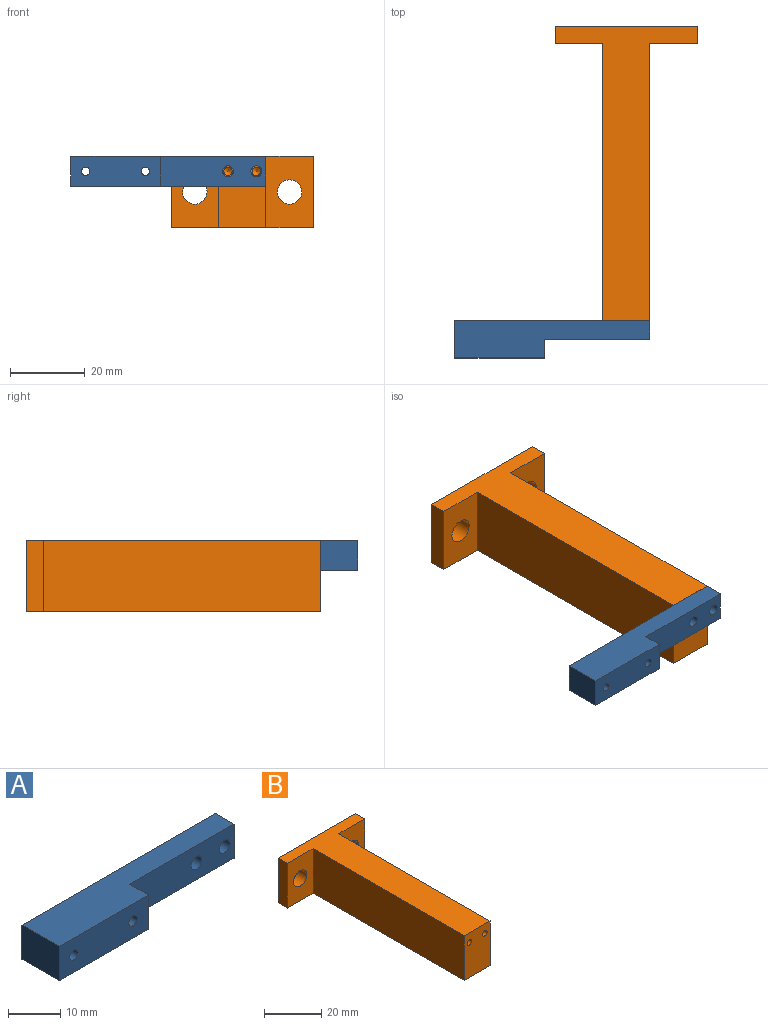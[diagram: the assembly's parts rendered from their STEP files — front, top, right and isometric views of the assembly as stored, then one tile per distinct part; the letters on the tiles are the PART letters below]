
ASSEMBLY  parts=2 mates=1
PART A: 12 faces, bbox 52.3x10x8 mm
  f0: plane 8x5mm, normal (1,0,0), area 40mm2, adj f1,f2,f3,f4
  f1: plane 52.32x10.01mm, normal (0,0,1), area 382.6mm2, adj f0,f3,f4,f5,f6,f7
  f2: plane 52.32x10.01mm, normal (0,0,-1), area 382.6mm2, adj f0,f3,f4,f5,f6,f7
  f3: plane 28.19x8mm, normal (0,-1,0), area 211.9mm2, adj f0,f1,f2,f5,f10,f11
  f4: plane 52.32x8mm, normal (0,1,0), area 397mm2, adj f0,f1,f2,f6,f8,f9,f10,f11
  f5: plane 8x5mm, normal (1,0,0), area 40mm2, adj f1,f2,f3,f7
  f6: plane 10.01x8mm, normal (-1,0,0), area 80.1mm2, adj f1,f2,f4,f7
  f7: plane 24.13x8mm, normal (0,-1,0), area 185mm2, adj f1,f2,f5,f6,f8,f9
  f8: cylinder r=1.13mm len=10.01mm, axis (0,1,0), area 71.1mm2, adj f4,f7
  f9: cylinder r=1.13mm len=10.01mm, axis (0,1,0), area 71.1mm2, adj f4,f7
  f10: cylinder r=1.47mm len=5mm, axis (0,-1,0), area 46.3mm2, adj f3,f4
  f11: cylinder r=1.47mm len=5mm, axis (0,-1,0), area 46.3mm2, adj f3,f4
PART B: 16 faces, bbox 38.1x79x19.1 mm
  f0: plane 19.05x12.7mm, normal (0,-1,0), area 208.5mm2, adj f1,f2,f3,f7,f15
  f1: plane 78.99x38.1mm, normal (0,0,-1), area 1119.4mm2, adj f0,f2,f4,f5,f6,f7,f8,f9
  f2: plane 19.05x4.57mm, normal (1,0,0), area 87.1mm2, adj f0,f1,f3,f5
  f3: plane 78.99x38.1mm, normal (0,0,1), area 1119.4mm2, adj f0,f2,f4,f5,f6,f7,f8,f9
  f4: plane 19.05x4.57mm, normal (-1,0,0), area 87.1mm2, adj f1,f3,f5,f6
  f5: plane 38.1x19.05mm, normal (0,1,0), area 658.9mm2, adj f1,f2,f3,f4,f14,f15
  f6: plane 19.05x12.7mm, normal (0,-1,0), area 208.5mm2, adj f1,f3,f4,f8,f14
  f7: plane 74.42x19.05mm, normal (1,0,0), area 1417.7mm2, adj f0,f1,f3,f9
  f8: plane 74.42x19.05mm, normal (-1,0,0), area 1417.7mm2, adj f1,f3,f6,f9
  f9: plane 19.05x12.7mm, normal (0,-1,0), area 233.9mm2, adj f1,f3,f7,f8,f11,f13
  f10: cone r=0mm half-angle=59deg, axis (0,-1,0), area 4.7mm2, adj f11
  f11: cylinder r=1.13mm len=15.45mm, axis (0,-1,0), area 109.7mm2, adj f9,f10
  f12: cone r=0mm half-angle=59deg, axis (0,-1,0), area 4.7mm2, adj f13
  f13: cylinder r=1.13mm len=15.45mm, axis (0,-1,0), area 109.7mm2, adj f9,f12
  f14: cylinder r=3.26mm len=6.53mm, axis (0,-1,0), area 93.8mm2, adj f5,f6
  f15: cylinder r=3.26mm len=6.53mm, axis (0,-1,0), area 93.8mm2, adj f0,f5
PLACE A t=(-16.75,-113.98,8.9)mm
PLACE B t=(-23.1,-39.56,-0.63)mm
MATE fastened B.f10 <-> A.f10  axis (0,-1,0) through (-19.29,-113.98,4.9)mm
